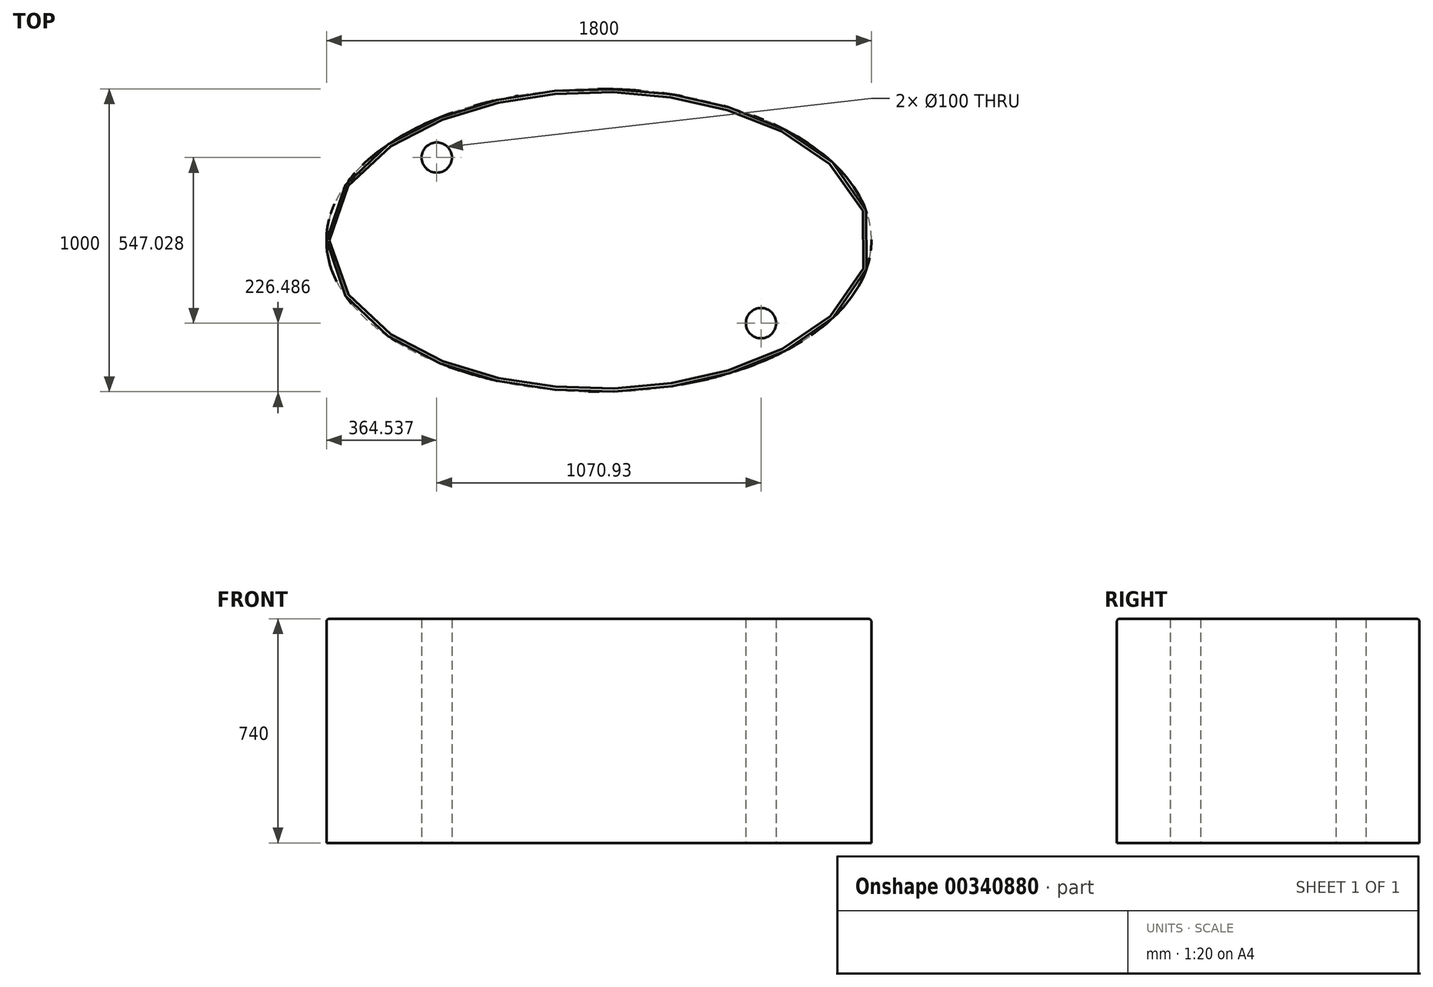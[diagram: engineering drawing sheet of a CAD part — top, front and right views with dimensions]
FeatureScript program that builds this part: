
annotation { "Feature Type Name" : "Feature", "Feature Type Description" : "" }
export const myFeature = defineFeature(function(context is Context, id is Id, definition is map)
    precondition{}
    {
        {
            var Q0;
            Q0=qCreatedBy(makeId("Top.planeOp"),FACE);
            var sketch = newSketch(context, id + "F0", { "sketchPlane" : qUnion([Q0])});
            skEllipse(sketch, "E0", {"center": v(0, 0) * mm, "majorRadius": 900 * mm, "minorRadius": 500 * mm, "majorAxis": v(-1, 0)});
            skLineSegment(sketch, "E1", {"start": v(0, 500) * mm, "end": v(0, -57.43) * mm, "construction": true});
            skPoint(sketch, "E1.endSnap0", {"position": v(0, -500) * mm});
            skLineSegment(sketch, "E2", {"start": v(-900, 0) * mm, "end": v(900, 0) * mm, "construction": true});
            skCircle(sketch, "E3", {"center": v(-535.46, -273.51) * mm, "radius": 50 * mm, "construction": true});
            skLineSegment(sketch, "E4.MirrorCS", {"start": v(0, -500) * mm, "end": v(0, 57.43) * mm, "construction": true});
            skCircle(sketch, "E5.MirrorC", {"center": v(-535.46, 273.51) * mm, "radius": 50 * mm});
            skCircle(sketch, "E6.MirrorC", {"center": v(-535.46, -273.51) * mm, "radius": 50 * mm});
            skCircle(sketch, "E7.MirrorC", {"center": v(535.46, 273.51) * mm, "radius": 50 * mm});
            skCircle(sketch, "E8.MirrorC", {"center": v(535.46, -273.51) * mm, "radius": 50 * mm});
            skSolve(sketch);
        }
        {
            var Q0;
            Q0=qSketchRegion(id+"F0",true);
            var Q1;
            Q1=makeQuery(id+"F0.imprint","IMPRINT",FACE,{"disambiguationData":[TD([[makeQuery(id+"F0.imprint","IMPRINT",EDGE,{"derivedFrom":sQuery(id+"F0.wireOp",EDGE,"E8.MirrorC")}),-1.0]])]});
            var Q2;
            Q2=makeQuery(id+"F0.imprint","IMPRINT",FACE,{"disambiguationData":[TD([[makeQuery(id+"F0.imprint","IMPRINT",EDGE,{"derivedFrom":sQuery(id+"F0.wireOp",EDGE,"E6.MirrorC")}),1.0]])]});
            var Q3;
            Q3=makeQuery(id+"F0.imprint","IMPRINT",FACE,{"disambiguationData":[TD([[makeQuery(id+"F0.imprint","IMPRINT",EDGE,{"derivedFrom":sQuery(id+"F0.wireOp",EDGE,"E5.MirrorC")}),-1.0]])]});
            var Q4;
            Q4=makeQuery(id+"F0.imprint","IMPRINT",FACE,{"disambiguationData":[TD([[makeQuery(id+"F0.imprint","IMPRINT",EDGE,{"derivedFrom":sQuery(id+"F0.wireOp",EDGE,"E7.MirrorC")}),1.0]])]});
            extrude(context, id + "F1", {"entities" : qUnion([Q0, Q1, Q2, Q3, Q4]), "depth" : 40 * mm});
        }
        {
            var Q0;
            Q0=makeQuery(id+"F0.imprint","IMPRINT",FACE,{"disambiguationData":[TD([[makeQuery(id+"F0.imprint","IMPRINT",EDGE,{"derivedFrom":sQuery(id+"F0.wireOp",EDGE,"E6.MirrorC")}),1.0]])]});
            var Q1;
            Q1=makeQuery(id+"F0.imprint","IMPRINT",FACE,{"disambiguationData":[TD([[makeQuery(id+"F0.imprint","IMPRINT",EDGE,{"derivedFrom":sQuery(id+"F0.wireOp",EDGE,"E5.MirrorC")}),-1.0]])]});
            var Q2;
            Q2=makeQuery(id+"F0.imprint","IMPRINT",FACE,{"disambiguationData":[TD([[makeQuery(id+"F0.imprint","IMPRINT",EDGE,{"derivedFrom":sQuery(id+"F0.wireOp",EDGE,"E7.MirrorC")}),1.0]])]});
            var Q3;
            Q3=makeQuery(id+"F0.imprint","IMPRINT",FACE,{"disambiguationData":[TD([[makeQuery(id+"F0.imprint","IMPRINT",EDGE,{"derivedFrom":sQuery(id+"F0.wireOp",EDGE,"E8.MirrorC")}),-1.0]])]});
            extrude(context, id + "F2", {"entities" : qUnion([Q0, Q1, Q2, Q3]), "operationType" : NewBodyOperationType.ADD, "oppositeDirection" : true, "depth" : 700 * mm});
        }
        {
            var Q0;
            Q0=makeQuery(id+"F1.opExtrude","CAP_EDGE",EDGE,{"disambiguationData":[OSD([sQuery(id+"F0.wireOp",EDGE,"E0")])],"isStart":false});
            var Q1;
            Q1=makeQuery(id+"F1.opExtrude","CAP_EDGE",EDGE,{"disambiguationData":[OSD([sQuery(id+"F0.wireOp",EDGE,"E0")])],"isStart":true});
            fillet(context, id + "F3", {"entities" : qUnion([Q0, Q1]), "radius" : 10 * mm, "tangentPropagation" : true, "allowEdgeOverflow" : false});
        }
    });
